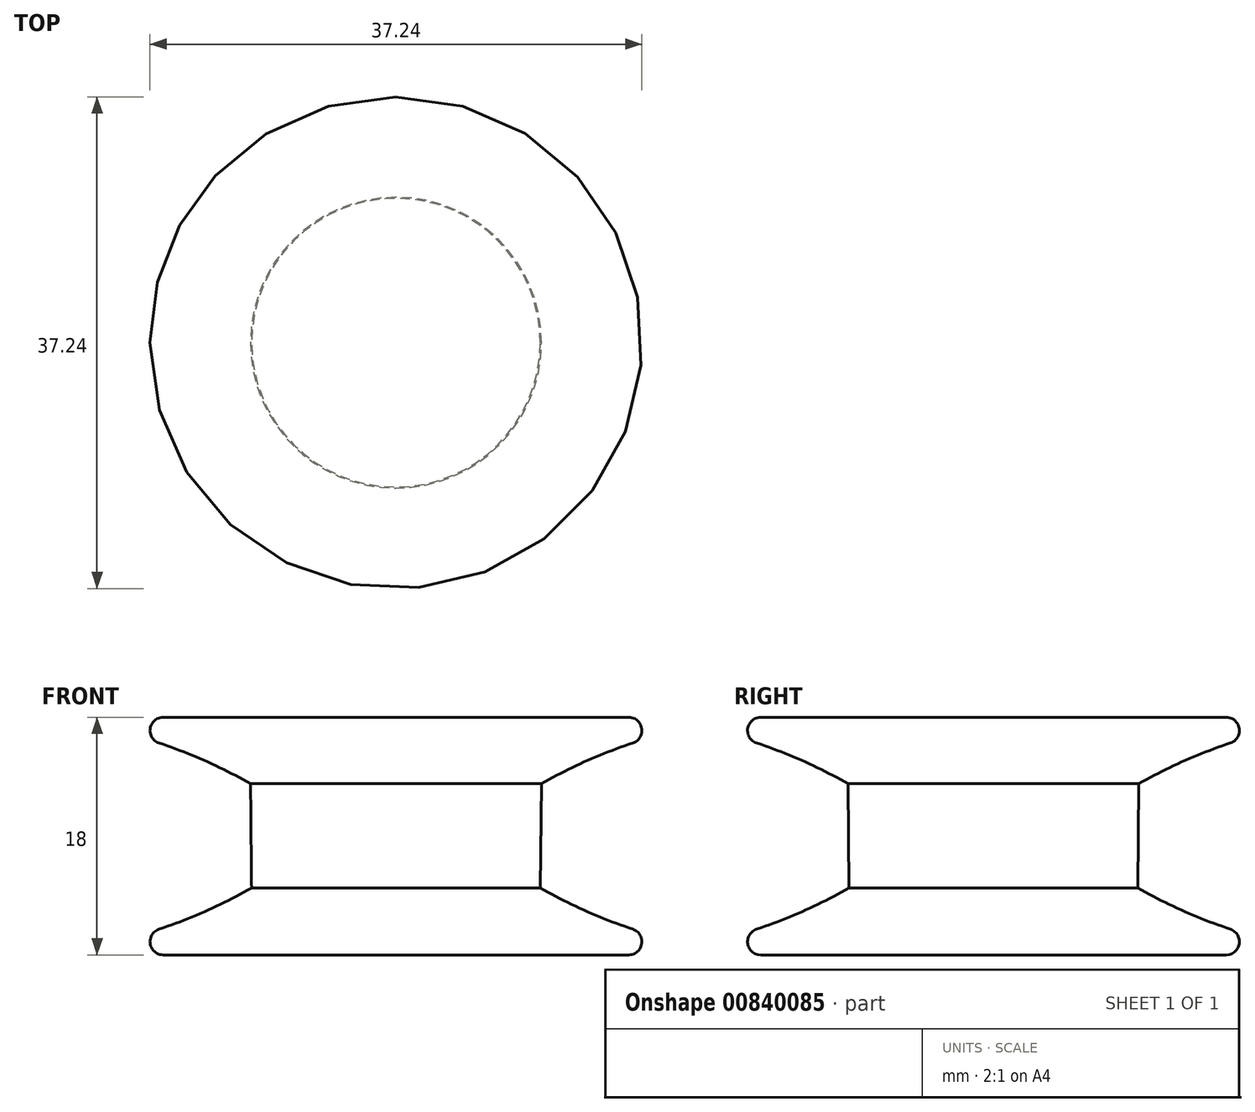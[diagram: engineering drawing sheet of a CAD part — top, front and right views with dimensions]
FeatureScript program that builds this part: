
annotation { "Feature Type Name" : "Feature", "Feature Type Description" : "" }
export const myFeature = defineFeature(function(context is Context, id is Id, definition is map)
    precondition{}
    {
        {
            var Q0;
            Q0=qCreatedBy(makeId("Front.planeOp"),FACE);
            var sketch = newSketch(context, id + "F0", { "sketchPlane" : qUnion([Q0])});
            skLineSegment(sketch, "E0", {"start": v(0, 0) * mm, "end": v(0, 9) * mm});
            skLineSegment(sketch, "E1", {"start": v(0, 9) * mm, "end": v(30, 9) * mm});
            skLineSegment(sketch, "E2", {"start": v(0, 0) * mm, "end": v(0, -9) * mm});
            skLineSegment(sketch, "E3", {"start": v(0, -9) * mm, "end": v(30, -9) * mm});
            skArc(sketch, "E4", {"start": v(30, 9) * mm, "mid": v(20.18, 7.72) * mm, "end": v(11, 3.96) * mm});
            skArc(sketch, "E5", {"start": v(10.93, -3.92) * mm, "mid": v(20.13, -7.7) * mm, "end": v(30, -9) * mm});
            skLineSegment(sketch, "E6", {"start": v(11, 3.96) * mm, "end": v(10.93, -3.92) * mm});
            skSolve(sketch);
        }
        {
            var Q0;
            Q0=makeQuery(id+"F0.imprint","IMPRINT",FACE,{"disambiguationData":[TD([[makeQuery(id+"F0.imprint","IMPRINT",EDGE,{"derivedFrom":sQuery(id+"F0.wireOp",EDGE,"E0")}),-1.0]])]});
            var Q1;
            Q1=sQuery(id+"F0.wireOp",EDGE,"E0");
            revolve(context, id + "F1", {"surfaceOperationType" : NewSurfaceOperationType.NEW, "entities" : qUnion([Q0]), "axis" : qUnion([Q1]), "revolveType" : RevolveType.FULL});
        }
        {
            var Q0;
            Q0=makeQuery(id+"F1.opRevolve","SWEPT_EDGE",EDGE,{"disambiguationData":[OSD([sQuery(id+"F0.wireOp",EDGE,"E1"),sQuery(id+"F0.wireOp",EDGE,"E4")])]});
            fillet(context, id + "F2", {"entities" : qUnion([Q0]), "radius" : 1 * mm, "tangentPropagation" : true, "allowEdgeOverflow" : false});
        }
        {
            var Q0;
            Q0=makeQuery(id+"F1.opRevolve","SWEPT_EDGE",EDGE,{"disambiguationData":[OSD([sQuery(id+"F0.wireOp",EDGE,"E3"),sQuery(id+"F0.wireOp",EDGE,"E5")])]});
            fillet(context, id + "F3", {"entities" : qUnion([Q0]), "radius" : 1 * mm, "tangentPropagation" : true, "allowEdgeOverflow" : false});
        }
    });
